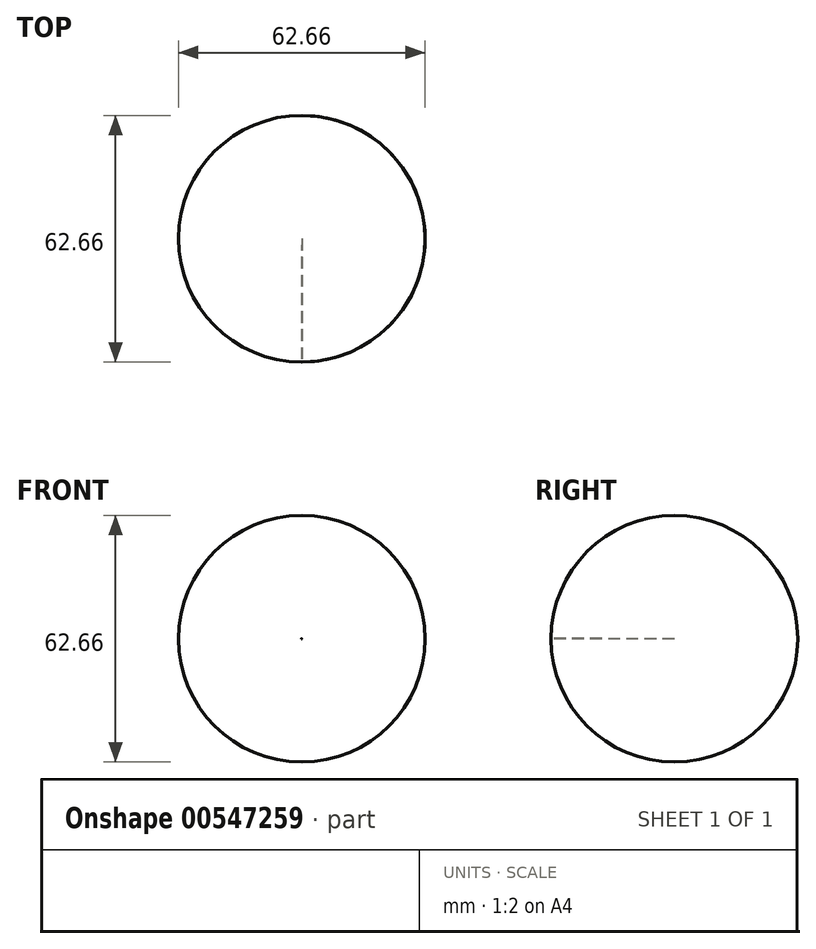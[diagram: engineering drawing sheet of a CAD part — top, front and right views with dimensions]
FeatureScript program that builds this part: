
annotation { "Feature Type Name" : "Feature", "Feature Type Description" : "" }
export const myFeature = defineFeature(function(context is Context, id is Id, definition is map)
    precondition{}
    {
        {
            var Q0;
            Q0=qCreatedBy(makeId("Top.planeOp"),FACE);
            var sketch = newSketch(context, id + "F0", { "sketchPlane" : qUnion([Q0])});
            skLineSegment(sketch, "E0", {"start": v(-44, 45.6) * mm, "end": v(-44, 14.26) * mm});
            skArc(sketch, "E1", {"start": v(-44, 14.26) * mm, "mid": v(-12.68, 45.56) * mm, "end": v(-43.96, 76.92) * mm});
            skLineSegment(sketch, "E2", {"start": v(-43.96, 76.92) * mm, "end": v(-44, 45.6) * mm});
            skSolve(sketch);
        }
        {
            var Q0;
            Q0=makeQuery(id+"F0.imprint","IMPRINT",FACE,{"disambiguationData":[TD([[makeQuery(id+"F0.imprint","IMPRINT",EDGE,{"derivedFrom":sQuery(id+"F0.wireOp",EDGE,"E0")}),1.0]])]});
            var Q1;
            Q1=sQuery(id+"F0.wireOp",EDGE,"E2");
            revolve(context, id + "F1", {"entities" : qUnion([Q0]), "axis" : qUnion([Q1]), "revolveType" : RevolveType.FULL});
        }
    });
